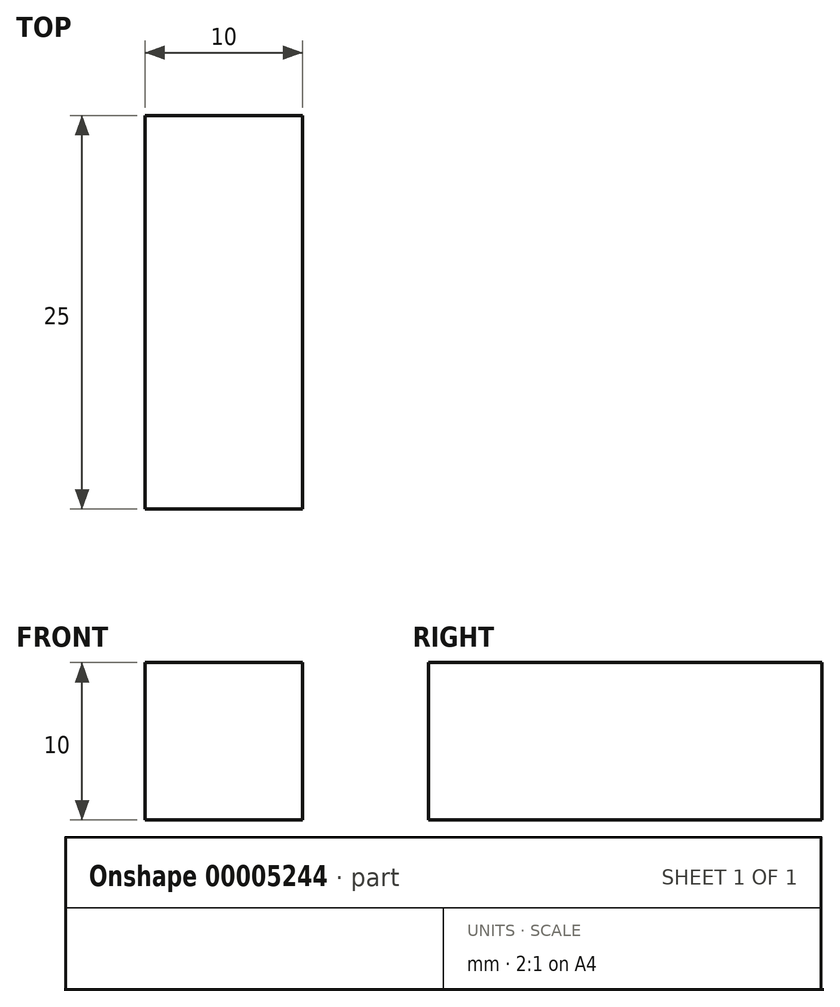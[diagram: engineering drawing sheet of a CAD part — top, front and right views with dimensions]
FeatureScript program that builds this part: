
annotation { "Feature Type Name" : "Feature", "Feature Type Description" : "" }
export const myFeature = defineFeature(function(context is Context, id is Id, definition is map)
    precondition{}
    {
        {
            var Q0;
            Q0=qCreatedBy(makeId("Front.planeOp"),FACE);
            var sketch = newSketch(context, id + "F0", { "sketchPlane" : qUnion([Q0])});
            skLineSegment(sketch, "E0.bottom", {"start": v(0, 0) * mm, "end": v(10, 0) * mm});
            skLineSegment(sketch, "E0.top", {"start": v(0, 10) * mm, "end": v(10, 10) * mm});
            skLineSegment(sketch, "E0.left", {"start": v(0, 0) * mm, "end": v(0, 10) * mm});
            skLineSegment(sketch, "E0.right", {"start": v(10, 0) * mm, "end": v(10, 10) * mm});
            skSolve(sketch);
        }
        {
            var Q0;
            Q0=makeQuery(id+"F0.imprint","IMPRINT",FACE,{"disambiguationData":[TD([[makeQuery(id+"F0.imprint","IMPRINT",EDGE,{"derivedFrom":sQuery(id+"F0.wireOp",EDGE,"E0.bottom")}),1.0]])]});
            extrude(context, id + "F1", {"entities" : qUnion([Q0]), "depth" : 25 * mm});
        }
    });
